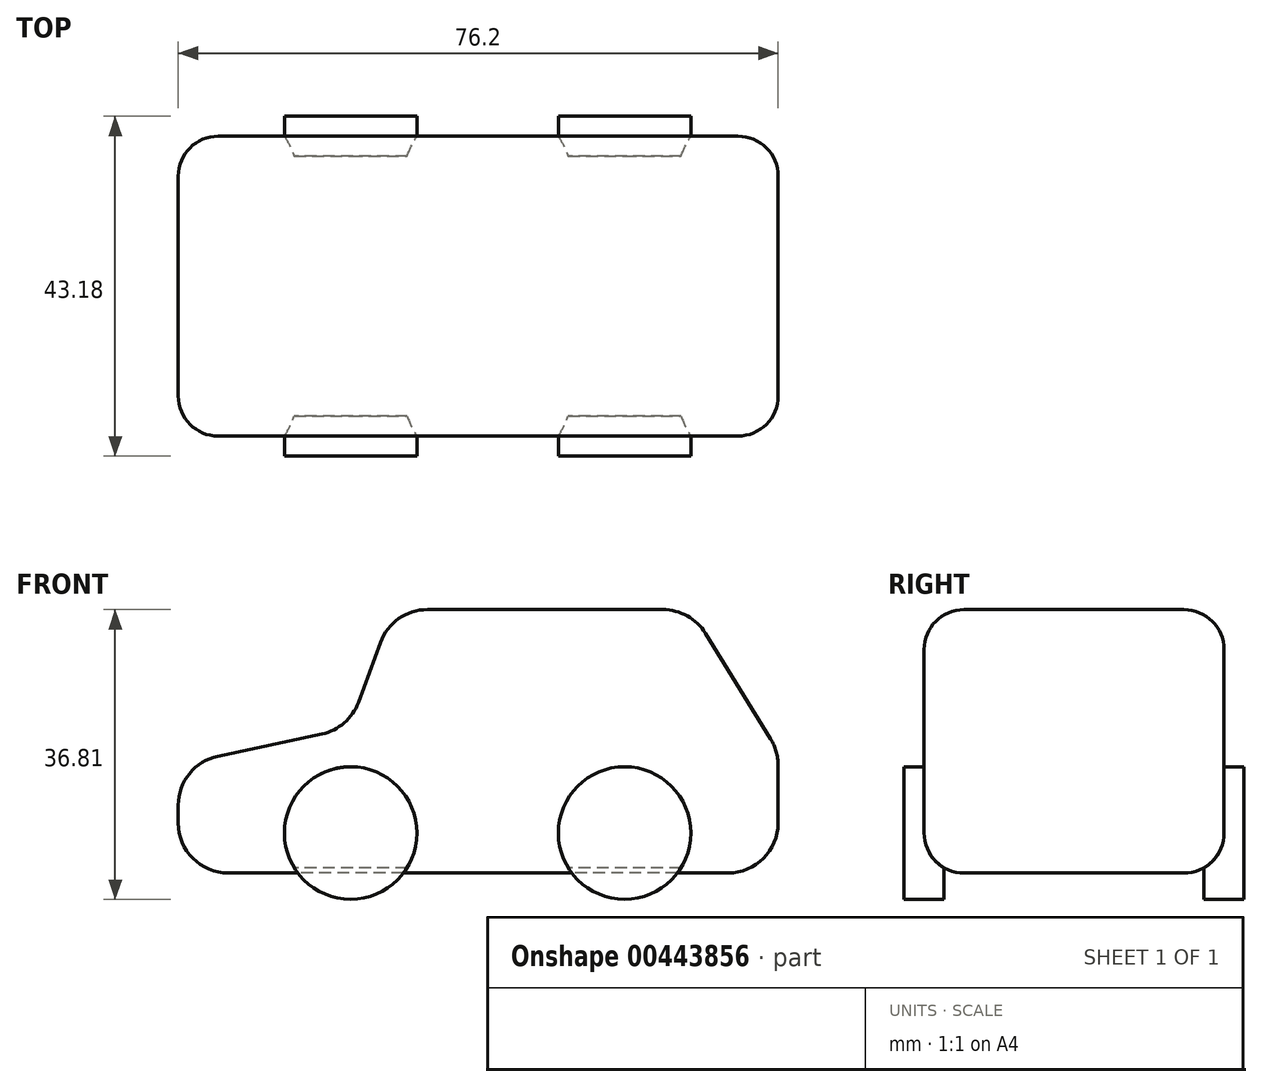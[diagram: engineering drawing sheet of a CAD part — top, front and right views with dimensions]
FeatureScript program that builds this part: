
annotation { "Feature Type Name" : "Feature", "Feature Type Description" : "" }
export const myFeature = defineFeature(function(context is Context, id is Id, definition is map)
    precondition{}
    {
        {
            var Q0;
            Q0=qCreatedBy(makeId("Front.planeOp"),FACE);
            var sketch = newSketch(context, id + "F0", { "sketchPlane" : qUnion([Q0])});
            skLineSegment(sketch, "E0", {"start": v(-45.02, 25.7) * mm, "end": v(-31.8, 28.52) * mm});
            skLineSegment(sketch, "E1", {"start": v(-27.16, 32.54) * mm, "end": v(-24.36, 40.17) * mm});
            skLineSegment(sketch, "E2", {"start": v(-18.4, 44.33) * mm, "end": v(11.53, 44.33) * mm});
            skLineSegment(sketch, "E3", {"start": v(16.93, 41.31) * mm, "end": v(25.2, 27.9) * mm});
            skLineSegment(sketch, "E4", {"start": v(26.15, 24.57) * mm, "end": v(26.15, 17.2) * mm});
            skLineSegment(sketch, "E5", {"start": v(19.8, 10.86) * mm, "end": v(-43.7, 10.86) * mm});
            skLineSegment(sketch, "E6", {"start": v(-50.05, 17.2) * mm, "end": v(-50.05, 19.5) * mm});
            skPoint(sketch, "E7.visualSharp", {"position": v(-28.37, 29.26) * mm});
            skArc(sketch, "E7.filletArc", {"start": v(-31.8, 28.52) * mm, "mid": v(-28.96, 29.94) * mm, "end": v(-27.16, 32.54) * mm});
            skPoint(sketch, "E8.visualSharp", {"position": v(-22.83, 44.33) * mm});
            skArc(sketch, "E8.filletArc", {"start": v(-18.4, 44.33) * mm, "mid": v(-22.03, 43.18) * mm, "end": v(-24.36, 40.17) * mm});
            skPoint(sketch, "E9.visualSharp", {"position": v(15.07, 44.33) * mm});
            skArc(sketch, "E9.filletArc", {"start": v(16.93, 41.31) * mm, "mid": v(14.62, 43.52) * mm, "end": v(11.53, 44.33) * mm});
            skPoint(sketch, "E10.visualSharp", {"position": v(26.15, 26.37) * mm});
            skArc(sketch, "E10.filletArc", {"start": v(26.15, 24.57) * mm, "mid": v(25.91, 26.3) * mm, "end": v(25.2, 27.9) * mm});
            skPoint(sketch, "E11.visualSharp", {"position": v(26.15, 10.86) * mm});
            skArc(sketch, "E11.filletArc", {"start": v(19.8, 10.86) * mm, "mid": v(24.3, 12.72) * mm, "end": v(26.15, 17.2) * mm});
            skPoint(sketch, "E12.visualSharp", {"position": v(-50.05, 10.86) * mm});
            skArc(sketch, "E12.filletArc", {"start": v(-50.05, 17.2) * mm, "mid": v(-48.19, 12.72) * mm, "end": v(-43.7, 10.86) * mm});
            skPoint(sketch, "E13.visualSharp", {"position": v(-50.05, 24.63) * mm});
            skArc(sketch, "E13.filletArc", {"start": v(-45.02, 25.7) * mm, "mid": v(-48.63, 23.48) * mm, "end": v(-50.05, 19.5) * mm});
            skSolve(sketch);
        }
        {
            var Q0;
            Q0=qSketchRegion(id+"F0",true);
            extrude(context, id + "F1", {"entities" : qUnion([Q0]), "endBound" : BoundingType.SYMMETRIC, "depth" : 38.1 * mm});
        }
        {
            var Q0;
            Q0=makeQuery(id+"F1.opExtrude","CAP_EDGE",EDGE,{"disambiguationData":[OSD([sQuery(id+"F0.wireOp",EDGE,"E2")])],"isStart":false});
            var Q1;
            Q1=makeQuery(id+"F1.opExtrude","CAP_EDGE",EDGE,{"disambiguationData":[OSD([sQuery(id+"F0.wireOp",EDGE,"E2")])],"isStart":true});
            fillet(context, id + "F2", {"entities" : qUnion([Q0, Q1]), "radius" : 5.08 * mm, "tangentPropagation" : true, "allowEdgeOverflow" : false});
        }
        {
            var Q0;
            Q0=makeQuery(id+"F1.opExtrude","CAP_FACE",FACE,{"disambiguationData":[OSD([sQuery(id+"F0.wireOp",EDGE,"E0"),sQuery(id+"F0.wireOp",EDGE,"E1"),sQuery(id+"F0.wireOp",EDGE,"E2"),sQuery(id+"F0.wireOp",EDGE,"E3"),sQuery(id+"F0.wireOp",EDGE,"E4"),sQuery(id+"F0.wireOp",EDGE,"E5"),sQuery(id+"F0.wireOp",EDGE,"E6"),sQuery(id+"F0.wireOp",EDGE,"E7.filletArc"),sQuery(id+"F0.wireOp",EDGE,"E8.filletArc"),sQuery(id+"F0.wireOp",EDGE,"E9.filletArc"),sQuery(id+"F0.wireOp",EDGE,"E10.filletArc"),sQuery(id+"F0.wireOp",EDGE,"E11.filletArc"),sQuery(id+"F0.wireOp",EDGE,"E12.filletArc"),sQuery(id+"F0.wireOp",EDGE,"E13.filletArc")])],"isStart":false});
            var sketch = newSketch(context, id + "F3", { "sketchPlane" : qUnion([Q0])});
            skCircle(sketch, "E14", {"center": v(-28.15, 15.94) * mm, "radius": 8.42 * mm});
            skCircle(sketch, "E15", {"center": v(6.65, 15.94) * mm, "radius": 8.42 * mm});
            skSolve(sketch);
        }
        {
            var Q0;
            {var subQ0=sQuery(id+"F3.wireOp",EDGE,"E15");var subQ1=sQuery(id+"F0.wireOp",EDGE,"E5");var subQ2=makeQuery(id+"F2.opFillet","BLEND_EDGE",EDGE,{"blendedFrom":[makeQuery(id+"F1.opExtrude","CAP_EDGE",EDGE,{"disambiguationData":[OSD([subQ1])],"isStart":false}),makeQuery(id+"F1.opExtrude","CAP_FACE",FACE,{"disambiguationData":[OSD([sQuery(id+"F0.wireOp",EDGE,"E0"),sQuery(id+"F0.wireOp",EDGE,"E1"),sQuery(id+"F0.wireOp",EDGE,"E2"),sQuery(id+"F0.wireOp",EDGE,"E3"),sQuery(id+"F0.wireOp",EDGE,"E4"),subQ1,sQuery(id+"F0.wireOp",EDGE,"E6"),sQuery(id+"F0.wireOp",EDGE,"E7.filletArc"),sQuery(id+"F0.wireOp",EDGE,"E8.filletArc"),sQuery(id+"F0.wireOp",EDGE,"E9.filletArc"),sQuery(id+"F0.wireOp",EDGE,"E10.filletArc"),sQuery(id+"F0.wireOp",EDGE,"E11.filletArc"),sQuery(id+"F0.wireOp",EDGE,"E12.filletArc"),sQuery(id+"F0.wireOp",EDGE,"E13.filletArc")])],"isStart":false})],"blendedInto":[makeQuery(id+"F1.opExtrude","CAP_FACE",FACE,{"disambiguationData":[OSD([sQuery(id+"F0.wireOp",EDGE,"E0"),sQuery(id+"F0.wireOp",EDGE,"E1"),sQuery(id+"F0.wireOp",EDGE,"E2"),sQuery(id+"F0.wireOp",EDGE,"E3"),sQuery(id+"F0.wireOp",EDGE,"E4"),subQ1,sQuery(id+"F0.wireOp",EDGE,"E6"),sQuery(id+"F0.wireOp",EDGE,"E7.filletArc"),sQuery(id+"F0.wireOp",EDGE,"E8.filletArc"),sQuery(id+"F0.wireOp",EDGE,"E9.filletArc"),sQuery(id+"F0.wireOp",EDGE,"E10.filletArc"),sQuery(id+"F0.wireOp",EDGE,"E11.filletArc"),sQuery(id+"F0.wireOp",EDGE,"E12.filletArc"),sQuery(id+"F0.wireOp",EDGE,"E13.filletArc")])],"isStart":false})]});var subQ3=makeQuery(id+"F3.imprint","INTERSECT",VERTEX,{"disambiguationData":[OD(0.0)],"derivedFrom":[subQ2,subQ0]});Q0=makeQuery(id+"F3.imprint","IMPRINT",FACE,{"disambiguationData":[TD([[makeQuery(id+"F3.imprint","IMPRINT",EDGE,{"disambiguationData":[TD([[subQ3,1.0]])],"derivedFrom":subQ0}),1.0]])]});}
            var Q1;
            {var subQ0=sQuery(id+"F3.wireOp",EDGE,"E15");var subQ1=sQuery(id+"F0.wireOp",EDGE,"E5");var subQ2=makeQuery(id+"F2.opFillet","BLEND_EDGE",EDGE,{"blendedFrom":[makeQuery(id+"F1.opExtrude","CAP_EDGE",EDGE,{"disambiguationData":[OSD([subQ1])],"isStart":false}),makeQuery(id+"F1.opExtrude","CAP_FACE",FACE,{"disambiguationData":[OSD([sQuery(id+"F0.wireOp",EDGE,"E0"),sQuery(id+"F0.wireOp",EDGE,"E1"),sQuery(id+"F0.wireOp",EDGE,"E2"),sQuery(id+"F0.wireOp",EDGE,"E3"),sQuery(id+"F0.wireOp",EDGE,"E4"),subQ1,sQuery(id+"F0.wireOp",EDGE,"E6"),sQuery(id+"F0.wireOp",EDGE,"E7.filletArc"),sQuery(id+"F0.wireOp",EDGE,"E8.filletArc"),sQuery(id+"F0.wireOp",EDGE,"E9.filletArc"),sQuery(id+"F0.wireOp",EDGE,"E10.filletArc"),sQuery(id+"F0.wireOp",EDGE,"E11.filletArc"),sQuery(id+"F0.wireOp",EDGE,"E12.filletArc"),sQuery(id+"F0.wireOp",EDGE,"E13.filletArc")])],"isStart":false})],"blendedInto":[makeQuery(id+"F1.opExtrude","CAP_FACE",FACE,{"disambiguationData":[OSD([sQuery(id+"F0.wireOp",EDGE,"E0"),sQuery(id+"F0.wireOp",EDGE,"E1"),sQuery(id+"F0.wireOp",EDGE,"E2"),sQuery(id+"F0.wireOp",EDGE,"E3"),sQuery(id+"F0.wireOp",EDGE,"E4"),subQ1,sQuery(id+"F0.wireOp",EDGE,"E6"),sQuery(id+"F0.wireOp",EDGE,"E7.filletArc"),sQuery(id+"F0.wireOp",EDGE,"E8.filletArc"),sQuery(id+"F0.wireOp",EDGE,"E9.filletArc"),sQuery(id+"F0.wireOp",EDGE,"E10.filletArc"),sQuery(id+"F0.wireOp",EDGE,"E11.filletArc"),sQuery(id+"F0.wireOp",EDGE,"E12.filletArc"),sQuery(id+"F0.wireOp",EDGE,"E13.filletArc")])],"isStart":false})]});var subQ3=makeQuery(id+"F3.imprint","INTERSECT",VERTEX,{"disambiguationData":[OD(0.0)],"derivedFrom":[subQ2,subQ0]});Q1=makeQuery(id+"F3.imprint","IMPRINT",FACE,{"disambiguationData":[TD([[makeQuery(id+"F3.imprint","IMPRINT",EDGE,{"disambiguationData":[TD([[subQ3,-1.0]])],"derivedFrom":subQ0}),1.0]])]});}
            var Q2;
            {var subQ0=sQuery(id+"F3.wireOp",EDGE,"E14");var subQ1=sQuery(id+"F0.wireOp",EDGE,"E7.filletArc");var subQ2=sQuery(id+"F0.wireOp",EDGE,"E0");var subQ3=makeQuery(id+"F1.opExtrude","CAP_FACE",FACE,{"disambiguationData":[OSD([subQ2,sQuery(id+"F0.wireOp",EDGE,"E1"),sQuery(id+"F0.wireOp",EDGE,"E2"),sQuery(id+"F0.wireOp",EDGE,"E3"),sQuery(id+"F0.wireOp",EDGE,"E4"),sQuery(id+"F0.wireOp",EDGE,"E5"),sQuery(id+"F0.wireOp",EDGE,"E6"),subQ1,sQuery(id+"F0.wireOp",EDGE,"E8.filletArc"),sQuery(id+"F0.wireOp",EDGE,"E9.filletArc"),sQuery(id+"F0.wireOp",EDGE,"E10.filletArc"),sQuery(id+"F0.wireOp",EDGE,"E11.filletArc"),sQuery(id+"F0.wireOp",EDGE,"E12.filletArc"),sQuery(id+"F0.wireOp",EDGE,"E13.filletArc")])],"isStart":false});var subQ4=makeQuery(id+"F2.opFillet","BLEND_EDGE",EDGE,{"blendedFrom":[makeQuery(id+"F1.opExtrude","CAP_EDGE",EDGE,{"disambiguationData":[OSD([subQ1])],"isStart":false}),subQ3],"blendedInto":[subQ3]});var subQ5=makeQuery(id+"F3.imprint","INTERSECT",VERTEX,{"derivedFrom":[subQ4,subQ0]});Q2=makeQuery(id+"F3.imprint","IMPRINT",FACE,{"disambiguationData":[TD([[makeQuery(id+"F3.imprint","IMPRINT",EDGE,{"disambiguationData":[TD([[subQ5,-1.0]])],"derivedFrom":subQ0}),1.0]])]});}
            var Q3;
            {var subQ0=sQuery(id+"F0.wireOp",EDGE,"E7.filletArc");var subQ1=sQuery(id+"F0.wireOp",EDGE,"E5");var subQ2=sQuery(id+"F0.wireOp",EDGE,"E0");var subQ3=makeQuery(id+"F1.opExtrude","CAP_FACE",FACE,{"disambiguationData":[OSD([subQ2,sQuery(id+"F0.wireOp",EDGE,"E1"),sQuery(id+"F0.wireOp",EDGE,"E2"),sQuery(id+"F0.wireOp",EDGE,"E3"),sQuery(id+"F0.wireOp",EDGE,"E4"),subQ1,sQuery(id+"F0.wireOp",EDGE,"E6"),subQ0,sQuery(id+"F0.wireOp",EDGE,"E8.filletArc"),sQuery(id+"F0.wireOp",EDGE,"E9.filletArc"),sQuery(id+"F0.wireOp",EDGE,"E10.filletArc"),sQuery(id+"F0.wireOp",EDGE,"E11.filletArc"),sQuery(id+"F0.wireOp",EDGE,"E12.filletArc"),sQuery(id+"F0.wireOp",EDGE,"E13.filletArc")])],"isStart":false});var subQ4=makeQuery(id+"F2.opFillet","BLEND_EDGE",EDGE,{"blendedFrom":[makeQuery(id+"F1.opExtrude","CAP_EDGE",EDGE,{"disambiguationData":[OSD([subQ0])],"isStart":false}),subQ3],"blendedInto":[subQ3]});var subQ7=sQuery(id+"F3.wireOp",EDGE,"E14");var subQ8=makeQuery(id+"F3.imprint","INTERSECT",VERTEX,{"derivedFrom":[subQ4,subQ7]});Q3=makeQuery(id+"F3.imprint","IMPRINT",FACE,{"disambiguationData":[TD([[makeQuery(id+"F3.imprint","IMPRINT",EDGE,{"disambiguationData":[TD([[subQ8,1.0]])],"derivedFrom":subQ7}),1.0]])]});}
            var Q4;
            {var subQ0=sQuery(id+"F3.wireOp",EDGE,"E14");var subQ1=sQuery(id+"F0.wireOp",EDGE,"E5");var subQ2=makeQuery(id+"F2.opFillet","BLEND_EDGE",EDGE,{"blendedFrom":[makeQuery(id+"F1.opExtrude","CAP_EDGE",EDGE,{"disambiguationData":[OSD([subQ1])],"isStart":false}),makeQuery(id+"F1.opExtrude","CAP_FACE",FACE,{"disambiguationData":[OSD([sQuery(id+"F0.wireOp",EDGE,"E0"),sQuery(id+"F0.wireOp",EDGE,"E1"),sQuery(id+"F0.wireOp",EDGE,"E2"),sQuery(id+"F0.wireOp",EDGE,"E3"),sQuery(id+"F0.wireOp",EDGE,"E4"),subQ1,sQuery(id+"F0.wireOp",EDGE,"E6"),sQuery(id+"F0.wireOp",EDGE,"E7.filletArc"),sQuery(id+"F0.wireOp",EDGE,"E8.filletArc"),sQuery(id+"F0.wireOp",EDGE,"E9.filletArc"),sQuery(id+"F0.wireOp",EDGE,"E10.filletArc"),sQuery(id+"F0.wireOp",EDGE,"E11.filletArc"),sQuery(id+"F0.wireOp",EDGE,"E12.filletArc"),sQuery(id+"F0.wireOp",EDGE,"E13.filletArc")])],"isStart":false})],"blendedInto":[makeQuery(id+"F1.opExtrude","CAP_FACE",FACE,{"disambiguationData":[OSD([sQuery(id+"F0.wireOp",EDGE,"E0"),sQuery(id+"F0.wireOp",EDGE,"E1"),sQuery(id+"F0.wireOp",EDGE,"E2"),sQuery(id+"F0.wireOp",EDGE,"E3"),sQuery(id+"F0.wireOp",EDGE,"E4"),subQ1,sQuery(id+"F0.wireOp",EDGE,"E6"),sQuery(id+"F0.wireOp",EDGE,"E7.filletArc"),sQuery(id+"F0.wireOp",EDGE,"E8.filletArc"),sQuery(id+"F0.wireOp",EDGE,"E9.filletArc"),sQuery(id+"F0.wireOp",EDGE,"E10.filletArc"),sQuery(id+"F0.wireOp",EDGE,"E11.filletArc"),sQuery(id+"F0.wireOp",EDGE,"E12.filletArc"),sQuery(id+"F0.wireOp",EDGE,"E13.filletArc")])],"isStart":false})]});var subQ3=makeQuery(id+"F3.imprint","INTERSECT",VERTEX,{"disambiguationData":[OD(0.0)],"derivedFrom":[subQ2,subQ0]});Q4=makeQuery(id+"F3.imprint","IMPRINT",FACE,{"disambiguationData":[TD([[makeQuery(id+"F3.imprint","IMPRINT",EDGE,{"disambiguationData":[TD([[subQ3,1.0]])],"derivedFrom":subQ0}),1.0]])]});}
            extrude(context, id + "F4", {"entities" : qUnion([Q0, Q1, Q2, Q3, Q4]), "operationType" : NewBodyOperationType.ADD, "endBound" : BoundingType.SYMMETRIC, "oppositeDirection" : true, "depth" : 5.08 * mm});
        }
        {
            var Q0;
            Q0=makeQuery(id+"F1.opExtrude","SWEPT_BODY",BODY,{"disambiguationData":[OSD([sQuery(id+"F0.wireOp",EDGE,"E0"),sQuery(id+"F0.wireOp",EDGE,"E1"),sQuery(id+"F0.wireOp",EDGE,"E2"),sQuery(id+"F0.wireOp",EDGE,"E3"),sQuery(id+"F0.wireOp",EDGE,"E4"),sQuery(id+"F0.wireOp",EDGE,"E5"),sQuery(id+"F0.wireOp",EDGE,"E6"),sQuery(id+"F0.wireOp",EDGE,"E7.filletArc"),sQuery(id+"F0.wireOp",EDGE,"E8.filletArc"),sQuery(id+"F0.wireOp",EDGE,"E9.filletArc"),sQuery(id+"F0.wireOp",EDGE,"E10.filletArc"),sQuery(id+"F0.wireOp",EDGE,"E11.filletArc"),sQuery(id+"F0.wireOp",EDGE,"E12.filletArc"),sQuery(id+"F0.wireOp",EDGE,"E13.filletArc")])]});
            var Q1;
            Q1=qCreatedBy(makeId("Front.planeOp"),FACE);
            mirror(context, id + "F5", {"operationType" : NewBodyOperationType.ADD, "entities" : qUnion([Q0]), "mirrorPlane" : qUnion([Q1])});
        }
    });
